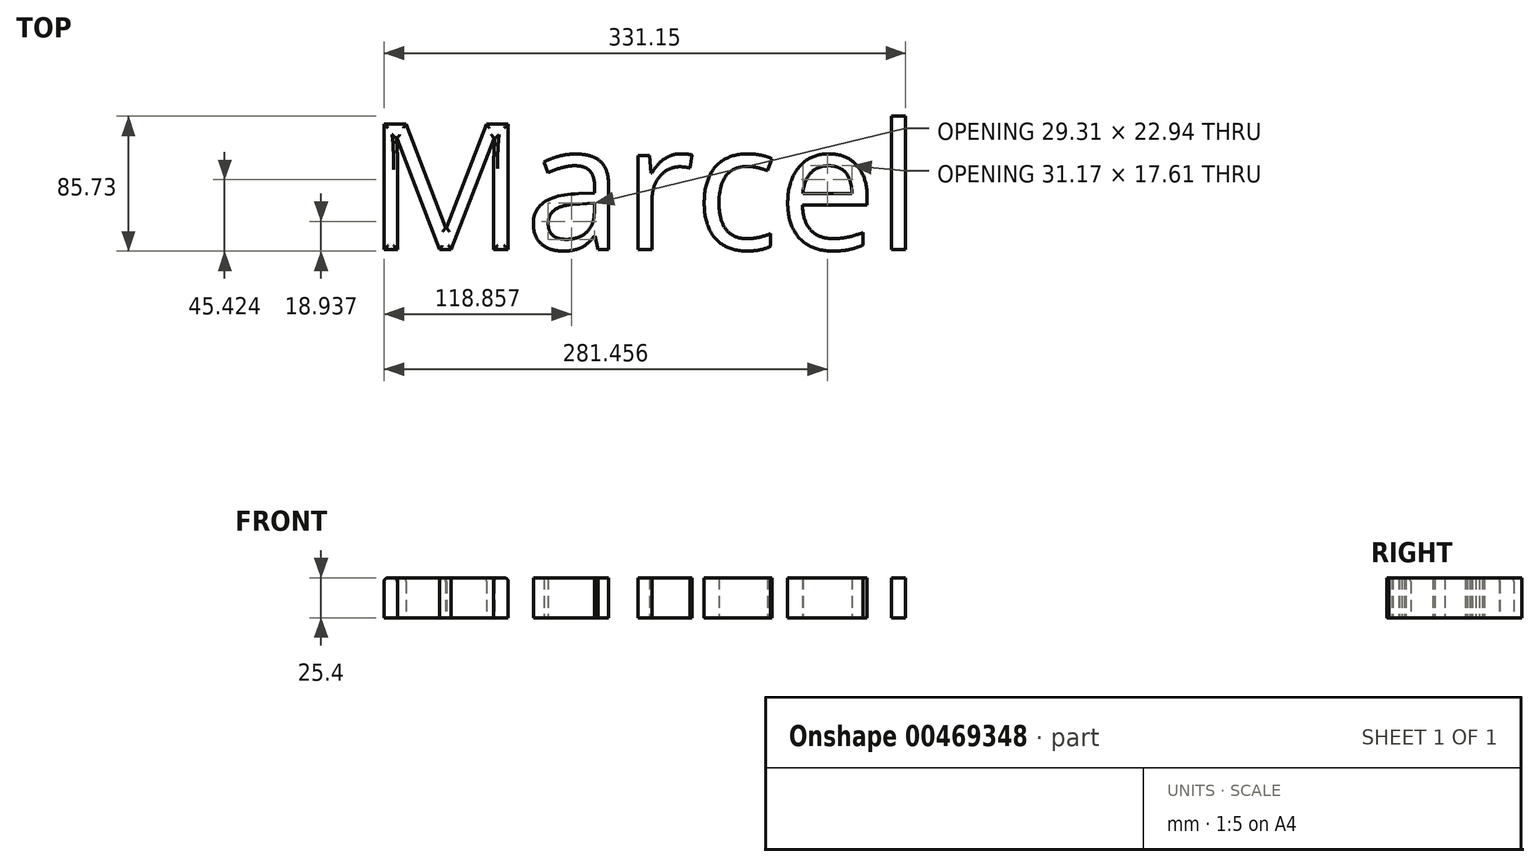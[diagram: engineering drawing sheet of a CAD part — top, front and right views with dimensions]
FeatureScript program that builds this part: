
annotation { "Feature Type Name" : "Feature", "Feature Type Description" : "" }
export const myFeature = defineFeature(function(context is Context, id is Id, definition is map)
    precondition{}
    {
        {
            var Q0;
            Q0=qCreatedBy(makeId("Top.planeOp"),FACE);
            var sketch = newSketch(context, id + "F0", { "sketchPlane" : qUnion([Q0])});
            skText(sketch, "E0", { "text": "Marcel", "fontName": "OpenSans-Regular.ttf"});
            const initialGuessF0  = {"E0": [-0.13565, -0.01675, 1, 0, 0.08019]};
            skSetInitialGuess(sketch, initialGuessF0);
            skSolve(sketch);
        }
        {
            var Q0;
            Q0 = qSketchRegion(id + "F0", true);
            extrude(context, id + "F1", {"entities" : qUnion([Q0]), "depth" : 25.4 * mm});
        }
        {
            var Q0;
            Q0=makeQuery(id+"F1.opExtrude","CAP_FACE",FACE,{"disambiguationData":[OSD([sQuery(id+"F0.wireOp",EDGE,"E0.sketch_text.stroke-0"),sQuery(id+"F0.wireOp",EDGE,"E0.sketch_text.stroke-1"),sQuery(id+"F0.wireOp",EDGE,"E0.sketch_text.stroke-2"),sQuery(id+"F0.wireOp",EDGE,"E0.sketch_text.stroke-3"),sQuery(id+"F0.wireOp",EDGE,"E0.sketch_text.stroke-4"),sQuery(id+"F0.wireOp",EDGE,"E0.sketch_text.stroke-5"),sQuery(id+"F0.wireOp",EDGE,"E0.sketch_text.stroke-6"),sQuery(id+"F0.wireOp",EDGE,"E0.sketch_text.stroke-7"),sQuery(id+"F0.wireOp",EDGE,"E0.sketch_text.stroke-8"),sQuery(id+"F0.wireOp",EDGE,"E0.sketch_text.stroke-9"),sQuery(id+"F0.wireOp",EDGE,"E0.sketch_text.stroke-10"),sQuery(id+"F0.wireOp",EDGE,"E0.sketch_text.stroke-11"),sQuery(id+"F0.wireOp",EDGE,"E0.sketch_text.stroke-12"),sQuery(id+"F0.wireOp",EDGE,"E0.sketch_text.stroke-13"),sQuery(id+"F0.wireOp",EDGE,"E0.sketch_text.stroke-14"),sQuery(id+"F0.wireOp",EDGE,"E0.sketch_text.stroke-15"),sQuery(id+"F0.wireOp",EDGE,"E0.sketch_text.stroke-16"),sQuery(id+"F0.wireOp",EDGE,"E0.sketch_text.stroke-17")])],"isStart":false});
            fillet(context, id + "F2", {"entities" : qUnion([Q0]), "radius" : 2.45 * mm, "tangentPropagation" : true, "allowEdgeOverflow" : false});
        }
    });
